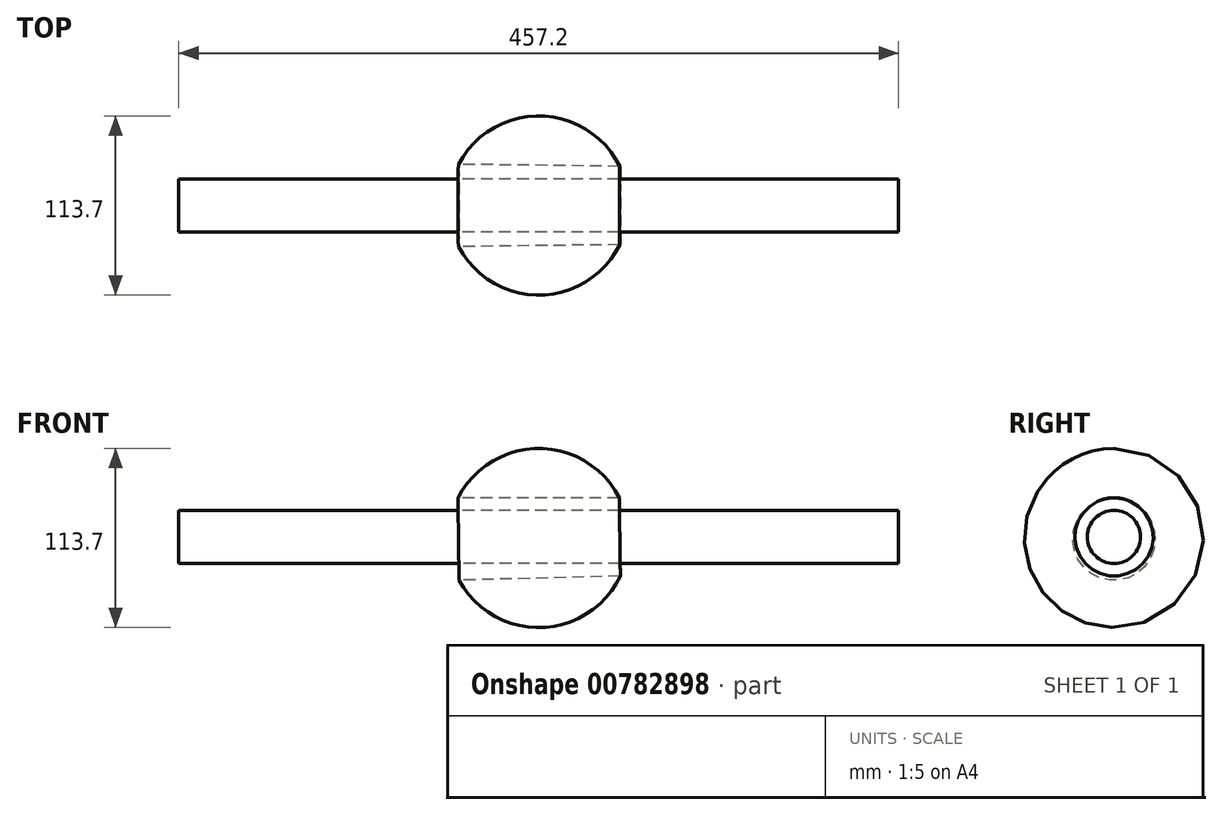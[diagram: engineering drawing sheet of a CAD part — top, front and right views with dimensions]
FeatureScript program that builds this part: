
annotation { "Feature Type Name" : "Feature", "Feature Type Description" : "" }
export const myFeature = defineFeature(function(context is Context, id is Id, definition is map)
    precondition{}
    {
        {
            var Q0;
            Q0=qCreatedBy(makeId("Front.planeOp"),FACE);
            var sketch = newSketch(context, id + "F0", { "sketchPlane" : qUnion([Q0])});
            skArc(sketch, "E0", {"start": v(-50.54, -27.53) * mm, "mid": v(1.5, -57.53) * mm, "end": v(51.9, -24.88) * mm});
            skLineSegment(sketch, "E1", {"start": v(-50.54, -27.53) * mm, "end": v(51.9, -24.88) * mm});
            skLineSegment(sketch, "E2", {"start": v(0, 0) * mm, "end": v(-56.96, -1.48) * mm, "construction": true});
            skLineSegment(sketch, "E3", {"start": v(-56.96, -1.48) * mm, "end": v(51.67, 0) * mm, "construction": true});
            skSolve(sketch);
        }
        {
            var Q0;
            Q0 = qSketchRegion(id + "F0", true);
            var Q1;
            Q1=sQuery(id+"F0.wireOp",EDGE,"E3");
            revolve(context, id + "F1", {"surfaceOperationType" : NewSurfaceOperationType.NEW, "entities" : qUnion([Q0]), "axis" : qUnion([Q1]), "revolveType" : RevolveType.FULL});
        }
        {
            var Q0;
            Q0=qCreatedBy(makeId("Right.planeOp"),FACE);
            var sketch = newSketch(context, id + "F2", { "sketchPlane" : qUnion([Q0])});
            skCircle(sketch, "E4", {"center": v(0, 0) * mm, "radius": 16.87 * mm});
            skSolve(sketch);
        }
        {
            var Q0;
            Q0 = qSketchRegion(id + "F2", true);
            var Q1;
            Q1=makeQuery(id+"F2.imprint","IMPRINT",FACE,{"disambiguationData":[TD([[makeQuery(id+"F2.imprint","IMPRINT",EDGE,{"derivedFrom":sQuery(id+"F2.wireOp",EDGE,"E4")}),1.0]])]});
            extrude(context, id + "F3", {"entities" : qUnion([Q0, Q1]), "endBound" : BoundingType.SYMMETRIC, "depth" : 457.2 * mm, "offsetDistance" : 25.4 * mm});
        }
    });
